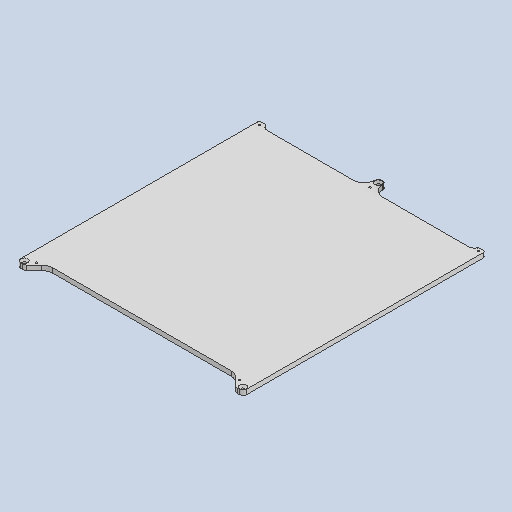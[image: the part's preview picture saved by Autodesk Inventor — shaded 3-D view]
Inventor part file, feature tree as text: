
AUTODESK INVENTOR PART (.ipt)
format: ipt  version: 2024.2 (Build 282272000, 272)  size: 105,984 bytes
history: native  units: in
note: dims shown in document units (in); Inventor stores cm internally (conversion verified against a paired STEP export)
features: fillet x1
ambient origin geometry x8: Origin, YZ Plane, XZ Plane, XY Plane, X Axis, Y Axis, Z Axis, Center Point
bodies: Solid1 (feature_tree)
feature tree (1):
  fillet  "Fillet6"  [1 undecoded]
note: 1 required parameter value undecoded (feature->parameter linkage not recoverable at this tier; creation-order binding heuristic only, values carry confidence <= 0.55)
